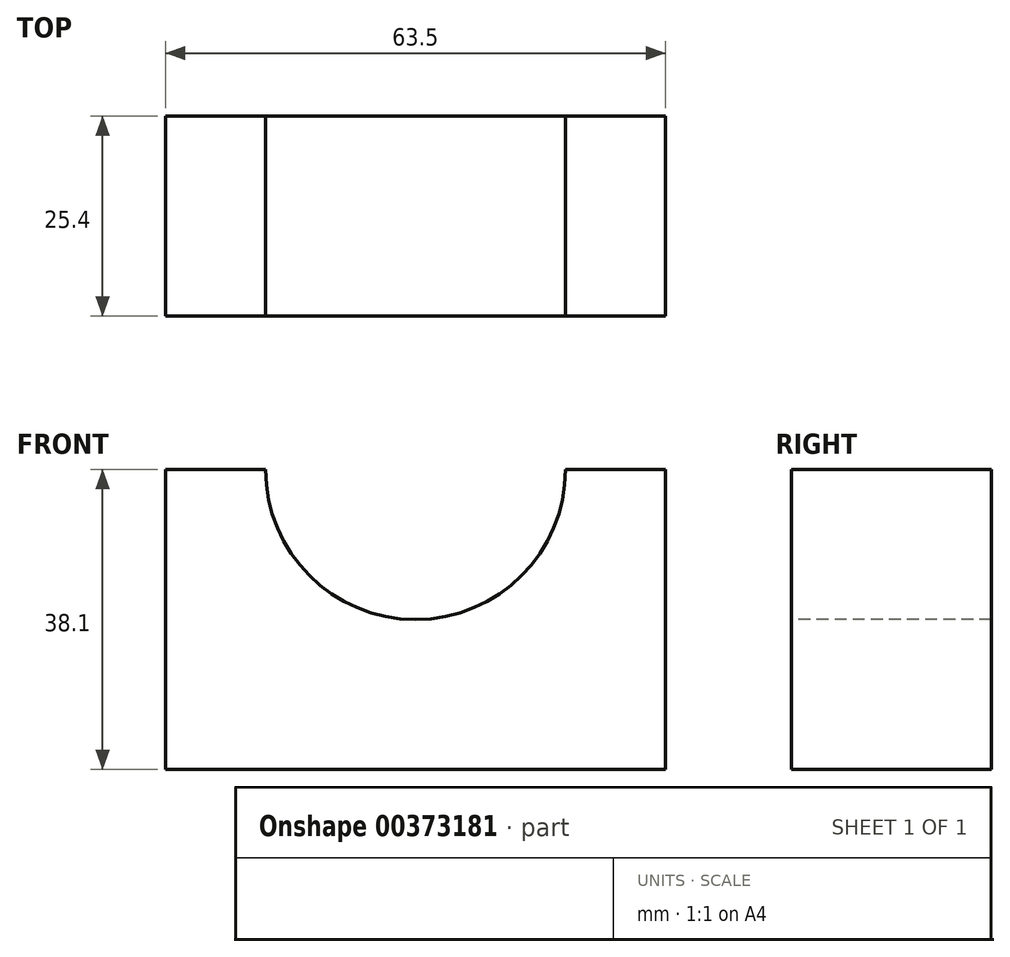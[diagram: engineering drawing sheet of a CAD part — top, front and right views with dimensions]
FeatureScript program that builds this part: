
annotation { "Feature Type Name" : "Feature", "Feature Type Description" : "" }
export const myFeature = defineFeature(function(context is Context, id is Id, definition is map)
    precondition{}
    {
        {
            var Q0;
            Q0=qCreatedBy(makeId("Front.planeOp"),FACE);
            var sketch = newSketch(context, id + "F0", { "sketchPlane" : qUnion([Q0])});
            skLineSegment(sketch, "E0", {"start": v(0, 0) * mm, "end": v(0, 38.1) * mm});
            skLineSegment(sketch, "E1", {"start": v(0, 38.1) * mm, "end": v(63.5, 38.1) * mm});
            skLineSegment(sketch, "E2", {"start": v(63.5, 38.1) * mm, "end": v(63.5, 0) * mm});
            skLineSegment(sketch, "E3", {"start": v(63.5, 0) * mm, "end": v(0, 0) * mm});
            skSolve(sketch);
        }
        {
            var Q0;
            Q0 = qSketchRegion(id + "F0", true);
            extrude(context, id + "F1", {"entities" : qUnion([Q0]), "depth" : 25.4 * mm});
        }
        {
            var Q0;
            Q0=makeQuery(id+"F1.opExtrude","CAP_FACE",FACE,{"disambiguationData":[OSD([sQuery(id+"F0.wireOp",EDGE,"E0"),sQuery(id+"F0.wireOp",EDGE,"E1"),sQuery(id+"F0.wireOp",EDGE,"E2"),sQuery(id+"F0.wireOp",EDGE,"E3")])],"isStart":false});
            var sketch = newSketch(context, id + "F2", { "sketchPlane" : qUnion([Q0])});
            skCircle(sketch, "E4", {"center": v(31.75, 38.1) * mm, "radius": 19.05 * mm});
            skSolve(sketch);
        }
        {
            var Q0;
            Q0 = qSketchRegion(id + "F2", true);
            extrude(context, id + "F3", {"entities" : qUnion([Q0]), "operationType" : NewBodyOperationType.REMOVE, "oppositeDirection" : true, "depth" : 25.4 * mm});
        }
    });
